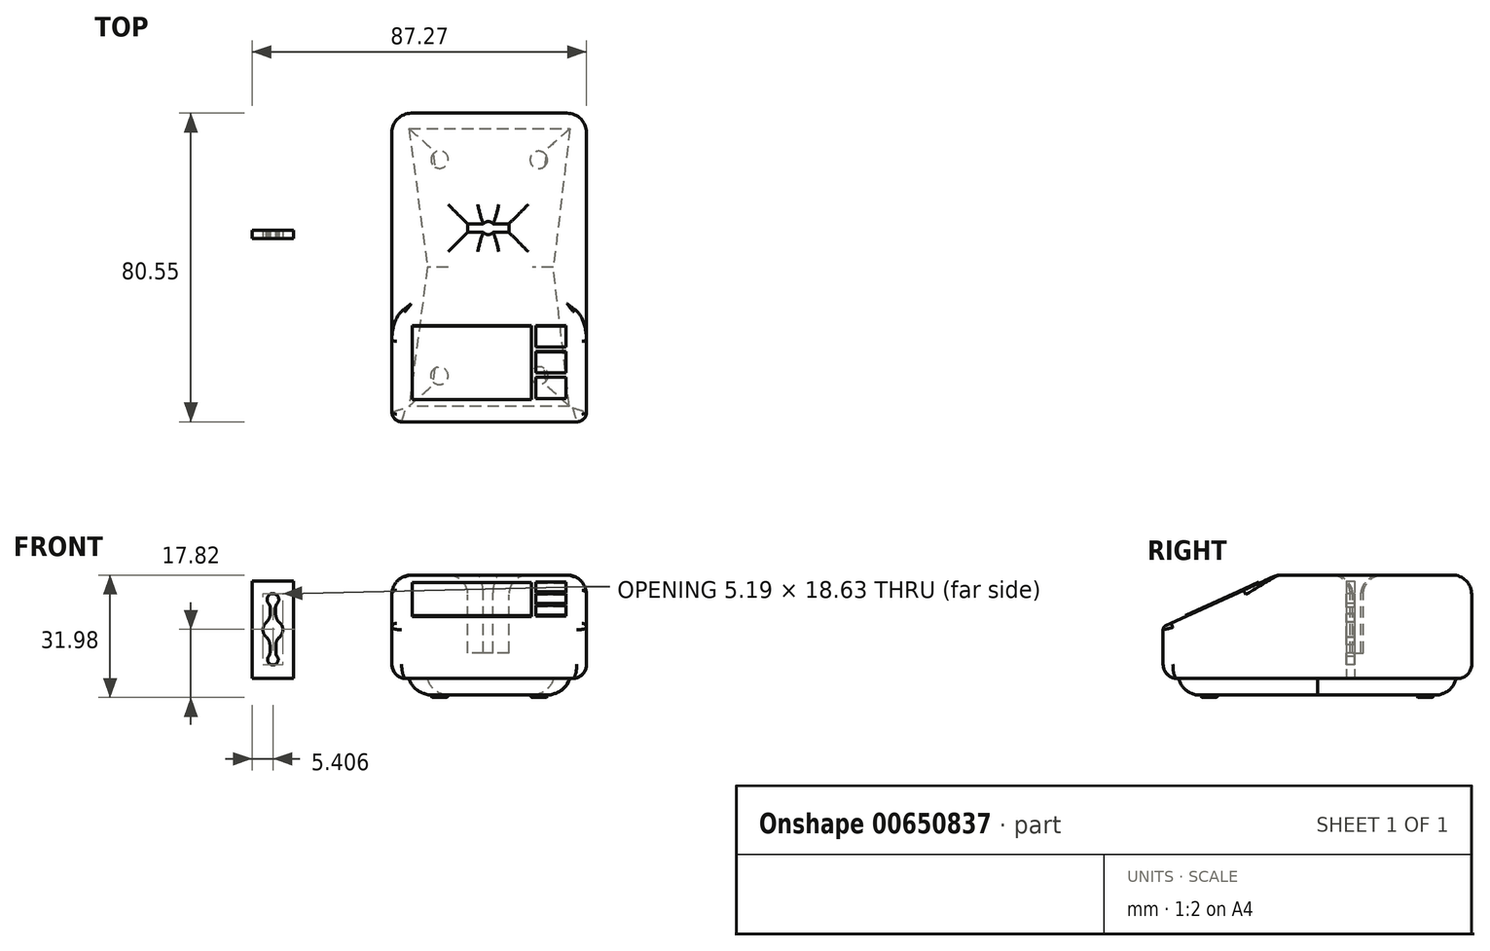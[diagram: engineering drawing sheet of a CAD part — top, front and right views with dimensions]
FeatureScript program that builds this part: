
annotation { "Feature Type Name" : "Feature", "Feature Type Description" : "" }
export const myFeature = defineFeature(function(context is Context, id is Id, definition is map)
    precondition{}
    {
        {
            var Q0;
            Q0=qCreatedBy(makeId("Right.planeOp"),FACE);
            var sketch = newSketch(context, id + "F0", { "sketchPlane" : qUnion([Q0])});
            skLineSegment(sketch, "E0.bottom", {"start": v(0, 27) * mm, "end": v(50.8, 27) * mm});
            skLineSegment(sketch, "E0.top", {"start": v(0, 0) * mm, "end": v(50.8, 0) * mm});
            skLineSegment(sketch, "E0.right", {"start": v(50.8, 27) * mm, "end": v(50.8, 3.3) * mm});
            skLineSegment(sketch, "E1.bottom", {"start": v(-29.75, 0) * mm, "end": v(0, 0) * mm});
            skLineSegment(sketch, "E1.left", {"start": v(-29.75, 3.3) * mm, "end": v(-29.75, 13.5) * mm});
            skLineSegment(sketch, "E2", {"start": v(0, 27) * mm, "end": v(-29.75, 13.5) * mm});
            skPoint(sketch, "E1.top.end.orphan", {"position": v(25.4, 3.3) * mm});
            skLineSegment(sketch, "E3", {"start": v(-29.75, 0) * mm, "end": v(-29.75, 3.3) * mm});
            skLineSegment(sketch, "E4", {"start": v(50.8, 3.3) * mm, "end": v(50.8, 0) * mm});
            skSolve(sketch);
        }
        {
            var Q0;
            Q0 = qSketchRegion(id + "F0", true);
            extrude(context, id + "F1", {"entities" : qUnion([Q0]), "endBound" : BoundingType.SYMMETRIC, "depth" : 50.8 * mm, "offsetDistance" : 25.4 * mm});
        }
        {
            var Q0;
            Q0=makeQuery(id+"F1.opExtrude","SWEPT_FACE",FACE,{"disambiguationData":[OSD([sQuery(id+"F0.wireOp",EDGE,"E2")])]});
            var sketch = newSketch(context, id + "F2", { "sketchPlane" : qUnion([Q0])});
            skLineSegment(sketch, "E5.bottom", {"start": v(11, -15.06) * mm, "end": v(-20.14, -15.06) * mm});
            skLineSegment(sketch, "E5.top", {"start": v(11, 5.99) * mm, "end": v(-20.14, 5.99) * mm});
            skLineSegment(sketch, "E5.left", {"start": v(11, -14.3) * mm, "end": v(11, 5.99) * mm});
            skLineSegment(sketch, "E5.right", {"start": v(-20.14, -14.3) * mm, "end": v(-20.14, 5.99) * mm});
            skLineSegment(sketch, "E6.bottom", {"start": v(12.22, 6.07) * mm, "end": v(20.07, 6.07) * mm});
            skLineSegment(sketch, "E6.top", {"start": v(12.22, 0) * mm, "end": v(20.07, 0) * mm});
            skLineSegment(sketch, "E6.left", {"start": v(12.22, 6.07) * mm, "end": v(12.22, 0) * mm});
            skLineSegment(sketch, "E6.right", {"start": v(20.07, 6.07) * mm, "end": v(20.07, 0) * mm});
            skLineSegment(sketch, "E7.1.0.0", {"start": v(12.2, -7.37) * mm, "end": v(20.05, -7.37) * mm});
            skLineSegment(sketch, "E7.1.0.1", {"start": v(12.2, -1.3) * mm, "end": v(12.2, -7.37) * mm});
            skLineSegment(sketch, "E7.1.0.2", {"start": v(12.2, -1.3) * mm, "end": v(20.05, -1.3) * mm});
            skLineSegment(sketch, "E7.1.0.3", {"start": v(20.05, -1.3) * mm, "end": v(20.05, -7.37) * mm});
            skLineSegment(sketch, "E7.2.0.0", {"start": v(12.17, -14.73) * mm, "end": v(20.02, -14.73) * mm});
            skLineSegment(sketch, "E7.2.0.1", {"start": v(12.17, -8.66) * mm, "end": v(12.17, -14.73) * mm});
            skLineSegment(sketch, "E7.2.0.2", {"start": v(12.17, -8.66) * mm, "end": v(20.02, -8.66) * mm});
            skLineSegment(sketch, "E7.2.0.3", {"start": v(20.02, -8.66) * mm, "end": v(20.02, -14.73) * mm});
            skLineSegment(sketch, "E7.direction1", {"start": v(12.22, 0) * mm, "end": v(12.2, -7.37) * mm, "construction": true});
            skLineSegment(sketch, "E8", {"start": v(-20.14, -15.06) * mm, "end": v(-20.14, -14.3) * mm});
            skLineSegment(sketch, "E9", {"start": v(11, -15.06) * mm, "end": v(11, -14.3) * mm});
            skSolve(sketch);
        }
        {
            var Q0;
            Q0 = qSketchRegion(id + "F2", true);
            extrude(context, id + "F3", {"entities" : qUnion([Q0]), "depth" : 0.25 * mm, "offsetDistance" : 25.4 * mm});
        }
        {
            var Q0;
            Q0=makeQuery(id+"F1.opExtrude","SWEPT_FACE",FACE,{"disambiguationData":[OSD([sQuery(id+"F0.wireOp",EDGE,"E0.bottom")])]});
            var sketch = newSketch(context, id + "F4", { "sketchPlane" : qUnion([Q0])});
            skLineSegment(sketch, "E10.bottom", {"start": v(5.16, 19.7) * mm, "end": v(-5.66, 19.7) * mm});
            skLineSegment(sketch, "E10.top", {"start": v(5.16, 21.93) * mm, "end": v(-5.66, 21.93) * mm});
            skLineSegment(sketch, "E10.left", {"start": v(5.16, 19.7) * mm, "end": v(5.16, 21.93) * mm});
            skLineSegment(sketch, "E10.right", {"start": v(-5.66, 19.7) * mm, "end": v(-5.66, 21.93) * mm});
            skPoint(sketch, "E10.middle", {"position": v(-0.25, 20.81) * mm});
            skCircle(sketch, "E11", {"center": v(-0.25, 20.81) * mm, "radius": 1.7 * mm});
            skSolve(sketch);
        }
        {
            var Q0;
            Q0 = qSketchRegion(id + "F4", true);
            extrude(context, id + "F5", {"entities" : qUnion([Q0]), "operationType" : NewBodyOperationType.REMOVE, "oppositeDirection" : true, "depth" : 20.32 * mm, "offsetDistance" : 25.4 * mm});
        }
        {
            var Q0;
            Q0=makeQuery(id+"F1.opExtrude","CAP_EDGE",EDGE,{"disambiguationData":[OSD([sQuery(id+"F0.wireOp",EDGE,"E1.left")])],"isStart":true});
            fillet(context, id + "F6", {"entities" : qUnion([Q0]), "radius" : 2.54 * mm, "tangentPropagation" : true, "allowEdgeOverflow" : false});
        }
        {
            var Q0;
            Q0=makeQuery(id+"F1.opExtrude","CAP_EDGE",EDGE,{"disambiguationData":[OSD([sQuery(id+"F0.wireOp",EDGE,"E1.left")])],"isStart":false});
            fillet(context, id + "F7", {"entities" : qUnion([Q0]), "radius" : 2.54 * mm, "tangentPropagation" : true, "allowEdgeOverflow" : false});
        }
        {
            var Q0;
            Q0=makeQuery(id+"F1.opExtrude","CAP_EDGE",EDGE,{"disambiguationData":[OSD([sQuery(id+"F0.wireOp",EDGE,"E0.right")])],"isStart":false});
            fillet(context, id + "F8", {"entities" : qUnion([Q0]), "radius" : 5.08 * mm, "tangentPropagation" : true, "allowEdgeOverflow" : false});
        }
        {
            var Q0;
            Q0=makeQuery(id+"F1.opExtrude","CAP_EDGE",EDGE,{"disambiguationData":[OSD([sQuery(id+"F0.wireOp",EDGE,"E0.right")])],"isStart":true});
            fillet(context, id + "F9", {"entities" : qUnion([Q0]), "radius" : 5.08 * mm, "tangentPropagation" : true, "allowEdgeOverflow" : false});
        }
        {
            var Q0;
            Q0=makeQuery(id+"F1.opExtrude","SWEPT_FACE",FACE,{"disambiguationData":[OSD([sQuery(id+"F0.wireOp",EDGE,"E0.bottom")])]});
            fillet(context, id + "F10", {"entities" : qUnion([Q0]), "radius" : 5.08 * mm, "tangentPropagation" : true, "allowEdgeOverflow" : false});
        }
        {
            var Q0;
            Q0=makeQuery(id+"F1.opExtrude","SWEPT_FACE",FACE,{"disambiguationData":[OSD([sQuery(id+"F0.wireOp",EDGE,"E0.top"),sQuery(id+"F0.wireOp",EDGE,"E1.bottom")])]});
            fillet(context, id + "F11", {"entities" : qUnion([Q0]), "radius" : 3.68 * mm, "tangentPropagation" : true, "allowEdgeOverflow" : false});
        }
        {
            var Q0;
            Q0=makeQuery(id+"F1.opExtrude","SWEPT_FACE",FACE,{"disambiguationData":[OSD([sQuery(id+"F0.wireOp",EDGE,"E0.top"),sQuery(id+"F0.wireOp",EDGE,"E1.bottom")])]});
            var sketch = newSketch(context, id + "F12", { "sketchPlane" : qUnion([Q0])});
            skLineSegment(sketch, "E12.bottom", {"start": v(20.94, 25.67) * mm, "end": v(-20.94, 25.67) * mm});
            skPoint(sketch, "E12.middle", {"position": v(0, 0) * mm});
            skLineSegment(sketch, "E13.top", {"start": v(-20.94, -46.76) * mm, "end": v(21.05, -46.76) * mm});
            skPoint(sketch, "E14", {"position": v(-16.14, -10.54) * mm});
            skLineSegment(sketch, "E15", {"start": v(-16.14, -10.54) * mm, "end": v(16.74, -10.54) * mm});
            skPoint(sketch, "E16", {"position": v(16.74, -10.54) * mm});
            skLineSegment(sketch, "E17", {"start": v(-16.14, -10.54) * mm, "end": v(-20.94, 25.67) * mm});
            skLineSegment(sketch, "E18", {"start": v(-20.94, -46.76) * mm, "end": v(-16.14, -10.54) * mm});
            skLineSegment(sketch, "E19", {"start": v(20.94, 25.67) * mm, "end": v(16.74, -10.54) * mm});
            skLineSegment(sketch, "E20", {"start": v(21.05, -46.76) * mm, "end": v(16.74, -10.54) * mm});
            skSolve(sketch);
        }
        {
            var Q0;
            Q0=makeQuery(id+"F12.imprint","IMPRINT",FACE,{"disambiguationData":[TD([[makeQuery(id+"F12.imprint","IMPRINT",EDGE,{"derivedFrom":sQuery(id+"F12.wireOp",EDGE,"E15")}),-1.0]])]});
            var Q1;
            Q1=makeQuery(id+"F12.imprint","IMPRINT",FACE,{"disambiguationData":[TD([[makeQuery(id+"F12.imprint","IMPRINT",EDGE,{"derivedFrom":sQuery(id+"F12.wireOp",EDGE,"E12.bottom")}),1.0]])]});
            extrude(context, id + "F13", {"entities" : qUnion([Q0, Q1]), "operationType" : NewBodyOperationType.ADD, "depth" : 4.32 * mm, "offsetDistance" : 25.4 * mm});
        }
        {
            var Q0;
            Q0=makeQuery(id+"F13.opExtrude","CAP_FACE",FACE,{"disambiguationData":[OSD([sQuery(id+"F0.wireOp",EDGE,"E0.top"),sQuery(id+"F0.wireOp",EDGE,"E0.right"),sQuery(id+"F0.wireOp",EDGE,"E1.bottom"),sQuery(id+"F12.wireOp",EDGE,"E12.bottom"),sQuery(id+"F12.wireOp",EDGE,"E13.top"),sQuery(id+"F12.wireOp",EDGE,"rkYKg8Y1-y552-My0n-W7Q7-vuoPP3TmxwOR"),sQuery(id+"F12.wireOp",EDGE,"zlAoThYX-KTOp-d1As-rref-19dZcvoEyOtx"),sQuery(id+"F12.wireOp",EDGE,"E17"),sQuery(id+"F12.wireOp",EDGE,"E18"),sQuery(id+"F12.wireOp",EDGE,"E19")])],"isStart":false});
            fillet(context, id + "F14", {"entities" : qUnion([Q0]), "radius" : 5.52 * mm, "tangentPropagation" : true, "allowEdgeOverflow" : false});
        }
        {
            var Q0;
            Q0=makeQuery(id+"F13.opExtrude","CAP_FACE",FACE,{"disambiguationData":[OSD([sQuery(id+"F12.wireOp",EDGE,"E12.bottom"),sQuery(id+"F12.wireOp",EDGE,"E12.left"),sQuery(id+"F12.wireOp",EDGE,"E12.right"),sQuery(id+"F12.wireOp",EDGE,"E13.top"),sQuery(id+"F12.wireOp",EDGE,"E13.left"),sQuery(id+"F12.wireOp",EDGE,"E13.right")])],"isStart":false});
            var sketch = newSketch(context, id + "F15", { "sketchPlane" : qUnion([Q0])});
            skCircle(sketch, "E21", {"center": v(-13, 17.75) * mm, "radius": 2.27 * mm});
            skCircle(sketch, "E22", {"center": v(13.11, 17.67) * mm, "radius": 2.27 * mm});
            skCircle(sketch, "E23", {"center": v(-12.93, -38.68) * mm, "radius": 2.27 * mm});
            skCircle(sketch, "E24", {"center": v(12.94, -38.62) * mm, "radius": 2.27 * mm});
            skSolve(sketch);
        }
        {
            var Q0;
            Q0 = qSketchRegion(id + "F15", true);
            extrude(context, id + "F16", {"entities" : qUnion([Q0]), "operationType" : NewBodyOperationType.ADD, "depth" : 0.66 * mm, "offsetDistance" : 25.4 * mm});
        }
        {
            var Q0;
            Q0=makeQuery(id+"F16.opExtrude","CAP_FACE",FACE,{"disambiguationData":[OSD([sQuery(id+"F15.wireOp",EDGE,"E21")])],"isStart":false});
            var Q1;
            Q1=makeQuery(id+"F16.opExtrude","CAP_FACE",FACE,{"disambiguationData":[OSD([sQuery(id+"F15.wireOp",EDGE,"E22")])],"isStart":false});
            var Q2;
            Q2=makeQuery(id+"F16.opExtrude","CAP_FACE",FACE,{"disambiguationData":[OSD([sQuery(id+"F15.wireOp",EDGE,"E23")])],"isStart":false});
            var Q3;
            Q3=makeQuery(id+"F16.opExtrude","CAP_FACE",FACE,{"disambiguationData":[OSD([sQuery(id+"F15.wireOp",EDGE,"E24")])],"isStart":false});
            fillet(context, id + "F17", {"entities" : qUnion([Q0, Q1, Q2, Q3]), "radius" : 0.8 * mm, "tangentPropagation" : true, "allowEdgeOverflow" : false});
        }
        {
            var Q0;
            Q0=makeQuery(id+"F1.opExtrude","CAP_EDGE",EDGE,{"disambiguationData":[OSD([sQuery(id+"F0.wireOp",EDGE,"E2")])],"isStart":true});
            fillet(context, id + "F18", {"entities" : qUnion([Q0]), "radius" : 1.23 * mm, "tangentPropagation" : true, "allowEdgeOverflow" : false});
        }
        {
            var Q0;
            Q0=qCreatedBy(makeId("Top.planeOp"),FACE);
            var sketch = newSketch(context, id + "F19", { "sketchPlane" : qUnion([Q0])});
            skLineSegment(sketch, "E25.bottom", {"start": v(-51.05, 18.02) * mm, "end": v(-61.87, 18.02) * mm});
            skLineSegment(sketch, "E25.top", {"start": v(-51.05, 20.25) * mm, "end": v(-61.87, 20.25) * mm});
            skLineSegment(sketch, "E25.left", {"start": v(-51.05, 18.02) * mm, "end": v(-51.05, 20.25) * mm});
            skLineSegment(sketch, "E25.right", {"start": v(-61.87, 18.02) * mm, "end": v(-61.87, 20.25) * mm});
            skPoint(sketch, "E25.middle", {"position": v(-56.46, 19.14) * mm});
            skSolve(sketch);
        }
        {
            var Q0;
            Q0=makeQuery(id+"F19.imprint","IMPRINT",FACE,{"disambiguationData":[TD([[makeQuery(id+"F19.imprint","IMPRINT",EDGE,{"derivedFrom":sQuery(id+"F19.wireOp",EDGE,"E25.bottom")}),-1.0]])]});
            extrude(context, id + "F20", {"entities" : qUnion([Q0]), "depth" : 25.4 * mm, "offsetDistance" : 25.4 * mm});
        }
        {
            var Q0;
            Q0=makeQuery(id+"F20.opExtrude","SWEPT_FACE",FACE,{"disambiguationData":[OSD([sQuery(id+"F19.wireOp",EDGE,"E25.bottom")])]});
            var sketch = newSketch(context, id + "F21", { "sketchPlane" : qUnion([Q0])});
            skPoint(sketch, "E26", {"position": v(-56.46, 25.4) * mm});
            skPoint(sketch, "E27", {"position": v(-56.46, 0) * mm});
            skPoint(sketch, "E28", {"position": v(-56.46, 12.7) * mm});
            skLineSegment(sketch, "E29", {"start": v(-61.87, 25.4) * mm, "end": v(-51.05, 25.4) * mm});
            skPoint(sketch, "E30", {"position": v(-56.46, 19.05) * mm});
            skLineSegment(sketch, "E31", {"start": v(-51.05, 0) * mm, "end": v(-61.87, 0) * mm});
            skPoint(sketch, "E32", {"position": v(-56.46, 6.35) * mm});
            skPoint(sketch, "E33.orphan", {"position": v(-61.87, 12.7) * mm});
            skPoint(sketch, "E34.end.orphan", {"position": v(-51.05, 12.7) * mm});
            skArc(sketch, "E35", {"start": v(-55.35, 19.57) * mm, "mid": v(-56.43, 22.16) * mm, "end": v(-57.63, 19.63) * mm});
            skArc(sketch, "E36", {"start": v(-57.56, 5.76) * mm, "mid": v(-56.46, 3.52) * mm, "end": v(-55.37, 5.77) * mm});
            skArc(sketch, "E37", {"start": v(-58.13, 14.68) * mm, "mid": v(-59.06, 12.68) * mm, "end": v(-58.1, 10.69) * mm});
            skLineSegment(sketch, "E38.left", {"start": v(-55.75, 18.52) * mm, "end": v(-55.75, 16.85) * mm});
            skLineSegment(sketch, "E38.right", {"start": v(-57.18, 18.5) * mm, "end": v(-57.18, 16.84) * mm});
            skPoint(sketch, "E38.middle", {"position": v(-56.46, 17.15) * mm});
            skLineSegment(sketch, "E39.left", {"start": v(-55.7, 8.77) * mm, "end": v(-55.7, 6.58) * mm});
            skLineSegment(sketch, "E39.right", {"start": v(-57.23, 8.83) * mm, "end": v(-57.23, 6.64) * mm});
            skPoint(sketch, "E39.middle", {"position": v(-56.46, 8.26) * mm});
            skPoint(sketch, "E40.orphan", {"position": v(-57.18, 15.03) * mm});
            skPoint(sketch, "E41.orphan", {"position": v(-55.75, 15.03) * mm});
            skPoint(sketch, "E42.orphan", {"position": v(-57.23, 10.86) * mm});
            skPoint(sketch, "E43.orphan", {"position": v(-55.7, 10.86) * mm});
            skArc(sketch, "E44.trimOffspring", {"start": v(-54.89, 10.64) * mm, "mid": v(-53.87, 12.67) * mm, "end": v(-54.84, 14.72) * mm});
            skPoint(sketch, "E39.top.end.orphan", {"position": v(-57.23, 5.67) * mm});
            skPoint(sketch, "E45.orphan", {"position": v(-55.7, 5.67) * mm});
            skArc(sketch, "E46", {"start": v(-57.23, 8.83) * mm, "mid": v(-57.55, 9.95) * mm, "end": v(-58.29, 10.86) * mm});
            skArc(sketch, "E47", {"start": v(-54.89, 10.64) * mm, "mid": v(-55.49, 9.77) * mm, "end": v(-55.7, 8.74) * mm});
            skArc(sketch, "E48", {"start": v(-55.75, 16.85) * mm, "mid": v(-55.5, 15.7) * mm, "end": v(-54.84, 14.72) * mm});
            skArc(sketch, "E49", {"start": v(-58.25, 14.58) * mm, "mid": v(-57.44, 15.65) * mm, "end": v(-57.18, 16.96) * mm});
            skArc(sketch, "E50", {"start": v(-57.56, 5.76) * mm, "mid": v(-57.33, 6.18) * mm, "end": v(-57.23, 6.64) * mm});
            skArc(sketch, "E51", {"start": v(-55.7, 6.58) * mm, "mid": v(-55.6, 6.15) * mm, "end": v(-55.37, 5.77) * mm});
            skArc(sketch, "E52", {"start": v(-55.35, 19.57) * mm, "mid": v(-55.64, 19.08) * mm, "end": v(-55.75, 18.52) * mm});
            skArc(sketch, "E53", {"start": v(-57.18, 18.5) * mm, "mid": v(-57.32, 19.1) * mm, "end": v(-57.63, 19.63) * mm});
            skPoint(sketch, "E54.orphan", {"position": v(-57.18, 19.27) * mm});
            skPoint(sketch, "E55.orphan", {"position": v(-55.75, 19.27) * mm});
            skSolve(sketch);
        }
        {
            var Q0;
            Q0=makeQuery(id+"F21.imprint","IMPRINT",FACE,{"disambiguationData":[TD([[makeQuery(id+"F21.imprint","IMPRINT",EDGE,{"derivedFrom":sQuery(id+"F21.wireOp",EDGE,"E35")}),1.0]])]});
            extrude(context, id + "F22", {"entities" : qUnion([Q0]), "operationType" : NewBodyOperationType.REMOVE, "oppositeDirection" : true, "depth" : 25.4 * mm, "offsetDistance" : 25.4 * mm});
        }
    });
